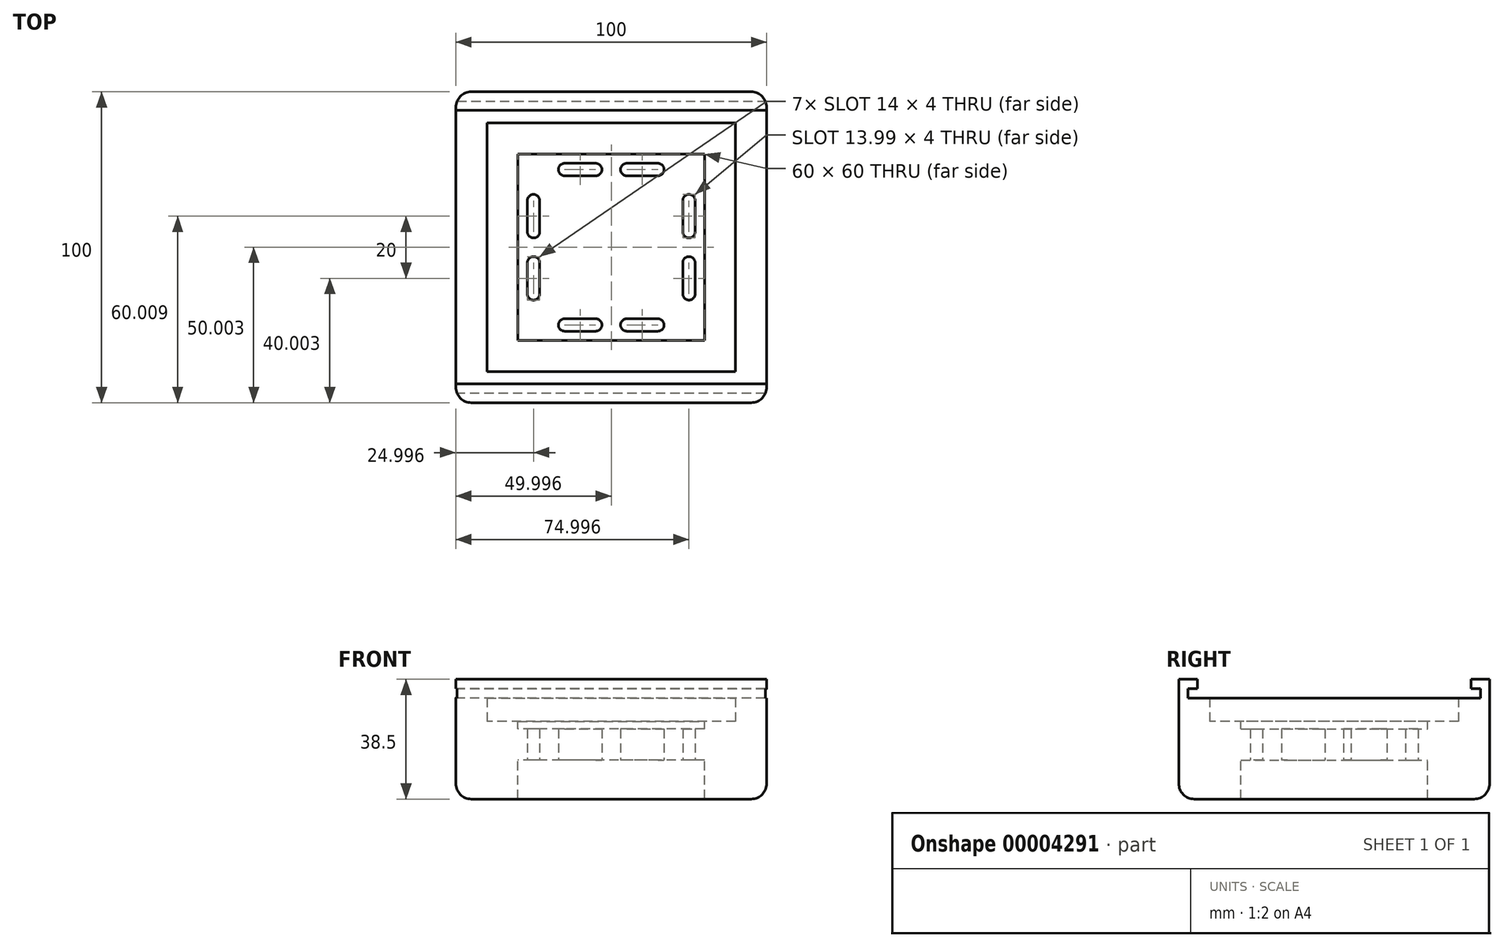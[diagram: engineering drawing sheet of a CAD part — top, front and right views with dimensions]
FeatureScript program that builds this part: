
annotation { "Feature Type Name" : "Feature", "Feature Type Description" : "" }
export const myFeature = defineFeature(function(context is Context, id is Id, definition is map)
    precondition{}
    {
        {
            var Q0;
            Q0=qCreatedBy(makeId("Top.planeOp"),FACE);
            var sketch = newSketch(context, id + "F0", { "sketchPlane" : qUnion([Q0])});
            skLineSegment(sketch, "E0", {"start": v(-127.44, -55.42) * mm, "end": v(-127.44, 44.58) * mm});
            skLineSegment(sketch, "E1", {"start": v(-127.44, 44.58) * mm, "end": v(-27.44, 44.58) * mm});
            skLineSegment(sketch, "E2", {"start": v(-27.44, 44.58) * mm, "end": v(-27.44, -55.42) * mm});
            skLineSegment(sketch, "E3", {"start": v(-27.44, -55.42) * mm, "end": v(-127.44, -55.42) * mm});
            skSolve(sketch);
        }
        {
            var Q0;
            Q0=makeQuery(id+"F0.imprint","IMPRINT",FACE,{"disambiguationData":[TD([[makeQuery(id+"F0.imprint","IMPRINT",EDGE,{"derivedFrom":sQuery(id+"F0.wireOp",EDGE,"E0")}),-1.0]])]});
            extrude(context, id + "F1", {"entities" : qUnion([Q0]), "depth" : 10 * mm});
        }
        {
            var Q0;
            Q0=makeQuery(id+"F1.opExtrude","CAP_FACE",FACE,{"disambiguationData":[OSD([sQuery(id+"F0.wireOp",EDGE,"E0"),sQuery(id+"F0.wireOp",EDGE,"E1"),sQuery(id+"F0.wireOp",EDGE,"E2"),sQuery(id+"F0.wireOp",EDGE,"E3")])],"isStart":false});
            var sketch = newSketch(context, id + "F2", { "sketchPlane" : qUnion([Q0])});
            skLineSegment(sketch, "E4.0", {"start": v(-117.44, 34.58) * mm, "end": v(-37.44, 34.58) * mm});
            skLineSegment(sketch, "E4.1", {"start": v(-117.44, -45.42) * mm, "end": v(-117.44, 34.58) * mm});
            skLineSegment(sketch, "E4.2", {"start": v(-37.44, -45.42) * mm, "end": v(-117.44, -45.42) * mm});
            skLineSegment(sketch, "E4.3", {"start": v(-37.44, 34.58) * mm, "end": v(-37.44, -45.42) * mm});
            skSolve(sketch);
        }
        {
            var Q0;
            Q0=makeQuery(id+"F2.imprint","IMPRINT",FACE,{"disambiguationData":[TD([[makeQuery(id+"F2.imprint","IMPRINT",EDGE,{"derivedFrom":sQuery(id+"F2.wireOp",EDGE,"E4.0")}),1.0]])]});
            extrude(context, id + "F3", {"entities" : qUnion([Q0]), "operationType" : NewBodyOperationType.ADD, "depth" : 10 * mm});
        }
        {
            var Q0;
            Q0=makeQuery(id+"F1.opExtrude","CAP_FACE",FACE,{"disambiguationData":[OSD([sQuery(id+"F0.wireOp",EDGE,"E0"),sQuery(id+"F0.wireOp",EDGE,"E1"),sQuery(id+"F0.wireOp",EDGE,"E2"),sQuery(id+"F0.wireOp",EDGE,"E3")])],"isStart":true});
            var sketch = newSketch(context, id + "F4", { "sketchPlane" : qUnion([Q0])});
            skLineSegment(sketch, "E5.0", {"start": v(-107.44, 35.42) * mm, "end": v(-107.44, -24.58) * mm});
            skLineSegment(sketch, "E5.1", {"start": v(-47.44, 35.42) * mm, "end": v(-107.44, 35.42) * mm});
            skLineSegment(sketch, "E5.2", {"start": v(-47.44, -24.58) * mm, "end": v(-47.44, 35.42) * mm});
            skLineSegment(sketch, "E5.3", {"start": v(-107.44, -24.58) * mm, "end": v(-47.44, -24.58) * mm});
            skLineSegment(sketch, "E6.0", {"start": v(-97.44, 25.42) * mm, "end": v(-97.44, -14.58) * mm});
            skLineSegment(sketch, "E6.1", {"start": v(-57.44, 25.42) * mm, "end": v(-97.44, 25.42) * mm});
            skLineSegment(sketch, "E6.2", {"start": v(-57.44, -14.58) * mm, "end": v(-57.44, 25.42) * mm});
            skLineSegment(sketch, "E6.3", {"start": v(-97.44, -14.58) * mm, "end": v(-57.44, -14.58) * mm});
            skSolve(sketch);
        }
        {
            var Q0;
            Q0=makeQuery(id+"F4.imprint","IMPRINT",FACE,{"disambiguationData":[TD([[makeQuery(id+"F4.imprint","IMPRINT",EDGE,{"derivedFrom":sQuery(id+"F4.wireOp",EDGE,"E5.0")}),-1.0]])]});
            extrude(context, id + "F5", {"entities" : qUnion([Q0]), "operationType" : NewBodyOperationType.ADD, "endBound" : BoundingType.SYMMETRIC, "depth" : 25 * mm});
        }
        {
            var Q0;
            Q0=makeQuery(id+"F1.opExtrude","CAP_FACE",FACE,{"disambiguationData":[OSD([sQuery(id+"F0.wireOp",EDGE,"E0"),sQuery(id+"F0.wireOp",EDGE,"E1"),sQuery(id+"F0.wireOp",EDGE,"E2"),sQuery(id+"F0.wireOp",EDGE,"E3")])],"isStart":true});
            var sketch = newSketch(context, id + "F6", { "sketchPlane" : qUnion([Q0])});
            skLineSegment(sketch, "E7.0", {"start": v(-62.44, 32.42) * mm, "end": v(-72.44, 32.42) * mm});
            skLineSegment(sketch, "E8.0", {"start": v(-104.44, 20.42) * mm, "end": v(-104.44, 10.42) * mm});
            skLineSegment(sketch, "E9.0", {"start": v(-100.44, 20.42) * mm, "end": v(-100.44, 10.42) * mm});
            skLineSegment(sketch, "E10.0", {"start": v(-92.44, -21.58) * mm, "end": v(-82.44, -21.58) * mm});
            skLineSegment(sketch, "E11", {"start": v(-107.44, 35.42) * mm, "end": v(-107.44, -24.58) * mm});
            skLineSegment(sketch, "E12", {"start": v(-107.44, -24.58) * mm, "end": v(-47.44, -24.58) * mm});
            skLineSegment(sketch, "E13", {"start": v(-47.44, -24.58) * mm, "end": v(-47.44, 35.42) * mm});
            skArc(sketch, "E14", {"start": v(-104.44, -9.58) * mm, "mid": v(-102.44, -11.58) * mm, "end": v(-100.44, -9.58) * mm});
            skArc(sketch, "E15", {"start": v(-100.44, 0.42) * mm, "mid": v(-102.44, 2.42) * mm, "end": v(-104.44, 0.42) * mm});
            skArc(sketch, "E16", {"start": v(-104.44, 10.42) * mm, "mid": v(-102.44, 8.42) * mm, "end": v(-100.44, 10.42) * mm});
            skArc(sketch, "E17", {"start": v(-100.44, 20.42) * mm, "mid": v(-102.44, 22.42) * mm, "end": v(-104.44, 20.42) * mm});
            skArc(sketch, "E18", {"start": v(-92.44, 32.42) * mm, "mid": v(-94.44, 30.42) * mm, "end": v(-92.44, 28.42) * mm});
            skArc(sketch, "E19", {"start": v(-82.44, 28.42) * mm, "mid": v(-80.44, 30.42) * mm, "end": v(-82.44, 32.42) * mm});
            skArc(sketch, "E20", {"start": v(-72.44, 32.42) * mm, "mid": v(-74.44, 30.42) * mm, "end": v(-72.44, 28.42) * mm});
            skArc(sketch, "E21", {"start": v(-62.44, 28.42) * mm, "mid": v(-60.44, 30.42) * mm, "end": v(-62.44, 32.42) * mm});
            skArc(sketch, "E22", {"start": v(-50.44, 20.42) * mm, "mid": v(-52.44, 22.42) * mm, "end": v(-54.44, 20.42) * mm});
            skArc(sketch, "E23", {"start": v(-54.44, 10.42) * mm, "mid": v(-52.44, 8.42) * mm, "end": v(-50.44, 10.42) * mm});
            skArc(sketch, "E24", {"start": v(-50.49, 0) * mm, "mid": v(-52.23, 2.4) * mm, "end": v(-54.44, 0.42) * mm});
            skArc(sketch, "E25", {"start": v(-54.44, -9.58) * mm, "mid": v(-52.44, -11.58) * mm, "end": v(-50.44, -9.57) * mm});
            skArc(sketch, "E26", {"start": v(-62.44, -21.58) * mm, "mid": v(-60.44, -19.58) * mm, "end": v(-62.44, -17.58) * mm});
            skArc(sketch, "E27", {"start": v(-72.44, -17.58) * mm, "mid": v(-74.44, -19.58) * mm, "end": v(-72.44, -21.58) * mm});
            skArc(sketch, "E28", {"start": v(-82.44, -21.58) * mm, "mid": v(-80.44, -19.58) * mm, "end": v(-82.44, -17.58) * mm});
            skArc(sketch, "E29", {"start": v(-92.44, -17.58) * mm, "mid": v(-94.44, -19.58) * mm, "end": v(-92.44, -21.58) * mm});
            skLineSegment(sketch, "E30.trimOffspring", {"start": v(-82.44, 32.42) * mm, "end": v(-92.44, 32.42) * mm});
            skLineSegment(sketch, "E31.trimOffspring", {"start": v(-82.44, 28.42) * mm, "end": v(-92.44, 28.42) * mm});
            skLineSegment(sketch, "E32.trimOffspring", {"start": v(-62.44, 28.42) * mm, "end": v(-72.44, 28.42) * mm});
            skLineSegment(sketch, "E33.trimOffspring", {"start": v(-54.44, 10.42) * mm, "end": v(-54.44, 20.42) * mm});
            skLineSegment(sketch, "E34.trimOffspring", {"start": v(-50.44, 10.42) * mm, "end": v(-50.44, 20.42) * mm});
            skLineSegment(sketch, "E35.trimOffspring", {"start": v(-72.44, -17.58) * mm, "end": v(-62.44, -17.58) * mm});
            skLineSegment(sketch, "E36.trimOffspring", {"start": v(-72.44, -21.58) * mm, "end": v(-62.44, -21.58) * mm});
            skLineSegment(sketch, "E37.trimOffspring", {"start": v(-92.44, -17.58) * mm, "end": v(-82.44, -17.58) * mm});
            skLineSegment(sketch, "E38.trimOffspring", {"start": v(-100.44, 0.42) * mm, "end": v(-100.44, -9.58) * mm});
            skLineSegment(sketch, "E39.trimOffspring", {"start": v(-104.44, 0.42) * mm, "end": v(-104.44, -9.58) * mm});
            skLineSegment(sketch, "E40", {"start": v(-54.44, 0.42) * mm, "end": v(-54.44, -9.58) * mm});
            skLineSegment(sketch, "E41", {"start": v(-50.49, 0) * mm, "end": v(-50.44, -9.57) * mm});
            skSolve(sketch);
        }
        {
            var Q0;
            Q0=makeQuery(id+"F6.imprint","IMPRINT",FACE,{"disambiguationData":[TD([[makeQuery(id+"F6.imprint","IMPRINT",EDGE,{"derivedFrom":sQuery(id+"F6.wireOp",EDGE,"E8.0")}),1.0]])]});
            var Q1;
            Q1=makeQuery(id+"F6.imprint","IMPRINT",FACE,{"disambiguationData":[TD([[makeQuery(id+"F6.imprint","IMPRINT",EDGE,{"derivedFrom":sQuery(id+"F6.wireOp",EDGE,"E18")}),1.0]])]});
            var Q2;
            Q2=makeQuery(id+"F6.imprint","IMPRINT",FACE,{"disambiguationData":[TD([[makeQuery(id+"F6.imprint","IMPRINT",EDGE,{"derivedFrom":sQuery(id+"F6.wireOp",EDGE,"E7.0")}),1.0]])]});
            var Q3;
            Q3=makeQuery(id+"F6.imprint","IMPRINT",FACE,{"disambiguationData":[TD([[makeQuery(id+"F6.imprint","IMPRINT",EDGE,{"derivedFrom":sQuery(id+"F6.wireOp",EDGE,"E22")}),1.0]])]});
            var Q4;
            Q4=makeQuery(id+"F6.imprint","IMPRINT",FACE,{"disambiguationData":[TD([[makeQuery(id+"F6.imprint","IMPRINT",EDGE,{"derivedFrom":sQuery(id+"F6.wireOp",EDGE,"E24")}),1.0]])]});
            var Q5;
            Q5=makeQuery(id+"F6.imprint","IMPRINT",FACE,{"disambiguationData":[TD([[makeQuery(id+"F6.imprint","IMPRINT",EDGE,{"derivedFrom":sQuery(id+"F6.wireOp",EDGE,"E26")}),1.0]])]});
            var Q6;
            Q6=makeQuery(id+"F6.imprint","IMPRINT",FACE,{"disambiguationData":[TD([[makeQuery(id+"F6.imprint","IMPRINT",EDGE,{"derivedFrom":sQuery(id+"F6.wireOp",EDGE,"E10.0")}),1.0]])]});
            var Q7;
            Q7=makeQuery(id+"F6.imprint","IMPRINT",FACE,{"disambiguationData":[TD([[makeQuery(id+"F6.imprint","IMPRINT",EDGE,{"derivedFrom":sQuery(id+"F6.wireOp",EDGE,"E14")}),1.0]])]});
            extrude(context, id + "F7", {"entities" : qUnion([Q0, Q1, Q2, Q3, Q4, Q5, Q6, Q7]), "operationType" : NewBodyOperationType.REMOVE, "oppositeDirection" : true, "depth" : 42.57 * mm});
        }
        {
            var Q0;
            Q0=makeQuery(id+"F3.opExtrude","CAP_FACE",FACE,{"disambiguationData":[OSD([sQuery(id+"F0.wireOp",EDGE,"E0"),sQuery(id+"F0.wireOp",EDGE,"E1"),sQuery(id+"F0.wireOp",EDGE,"E2"),sQuery(id+"F0.wireOp",EDGE,"E3"),sQuery(id+"F2.wireOp",EDGE,"E4.0"),sQuery(id+"F2.wireOp",EDGE,"E4.1"),sQuery(id+"F2.wireOp",EDGE,"E4.2"),sQuery(id+"F2.wireOp",EDGE,"E4.3")])],"isStart":false});
            var sketch = newSketch(context, id + "F8", { "sketchPlane" : qUnion([Q0])});
            skLineSegment(sketch, "E42.0", {"start": v(-27.44, -52.42) * mm, "end": v(-127.44, -52.42) * mm});
            skLineSegment(sketch, "E43.0", {"start": v(-127.44, 41.58) * mm, "end": v(-27.44, 41.58) * mm});
            skSolve(sketch);
        }
        {
            var Q0;
            {var subQ1=sQuery(id+"F8.wireOp",EDGE,"E42.0");Q0=makeQuery(id+"F8.imprint","IMPRINT",FACE,{"disambiguationData":[TD([[makeQuery(id+"F8.imprint","IMPRINT",EDGE,{"derivedFrom":subQ1}),1.0]])]});}
            var Q1;
            {var subQ1=sQuery(id+"F8.wireOp",EDGE,"E43.0");Q1=makeQuery(id+"F8.imprint","IMPRINT",FACE,{"disambiguationData":[TD([[makeQuery(id+"F8.imprint","IMPRINT",EDGE,{"derivedFrom":subQ1}),1.0]])]});}
            extrude(context, id + "F9", {"entities" : qUnion([Q0, Q1]), "operationType" : NewBodyOperationType.ADD, "depth" : 6 * mm});
        }
        {
            var Q0;
            Q0=makeQuery(id+"F9.opExtrude","SWEPT_FACE",FACE,{"disambiguationData":[OSD([sQuery(id+"F8.wireOp",EDGE,"E43.0")])]});
            var sketch = newSketch(context, id + "F10", { "sketchPlane" : qUnion([Q0])});
            skLineSegment(sketch, "E44.0", {"start": v(-127.44, 23) * mm, "end": v(-27.44, 23) * mm});
            skSolve(sketch);
        }
        {
            var Q0;
            {var subQ2=sQuery(id+"F10.wireOp",EDGE,"E44.0");Q0=makeQuery(id+"F10.imprint","IMPRINT",FACE,{"disambiguationData":[TD([[makeQuery(id+"F10.imprint","IMPRINT",EDGE,{"derivedFrom":subQ2}),1.0]])]});}
            extrude(context, id + "F11", {"entities" : qUnion([Q0]), "operationType" : NewBodyOperationType.ADD, "depth" : 3 * mm});
        }
        {
            var Q0;
            Q0=makeQuery(id+"F9.opExtrude","SWEPT_FACE",FACE,{"disambiguationData":[OSD([sQuery(id+"F8.wireOp",EDGE,"E42.0")])]});
            var sketch = newSketch(context, id + "F12", { "sketchPlane" : qUnion([Q0])});
            skLineSegment(sketch, "E45.0", {"start": v(27.44, 23) * mm, "end": v(127.44, 23) * mm});
            skSolve(sketch);
        }
        {
            var Q0;
            {var subQ2=sQuery(id+"F12.wireOp",EDGE,"E45.0");Q0=makeQuery(id+"F12.imprint","IMPRINT",FACE,{"disambiguationData":[TD([[makeQuery(id+"F12.imprint","IMPRINT",EDGE,{"derivedFrom":subQ2}),1.0]])]});}
            extrude(context, id + "F13", {"entities" : qUnion([Q0]), "operationType" : NewBodyOperationType.ADD, "depth" : 3 * mm});
        }
        {
            var Q0;
            Q0=makeQuery(id+"F5.opExtrude","CAP_EDGE",EDGE,{"disambiguationData":[OSD([sQuery(id+"F0.wireOp",EDGE,"E3")])],"isStart":false});
            var Q1;
            Q1=makeQuery(id+"F5.opExtrude","CAP_EDGE",EDGE,{"disambiguationData":[OSD([sQuery(id+"F0.wireOp",EDGE,"E2")])],"isStart":false});
            var Q2;
            Q2=makeQuery(id+"F5.opExtrude","CAP_EDGE",EDGE,{"disambiguationData":[OSD([sQuery(id+"F0.wireOp",EDGE,"E1")])],"isStart":false});
            var Q3;
            Q3=makeQuery(id+"F5.opExtrude","CAP_EDGE",EDGE,{"disambiguationData":[OSD([sQuery(id+"F0.wireOp",EDGE,"E0")])],"isStart":false});
            fillet(context, id + "F14", {"entities" : qUnion([Q0, Q1, Q2, Q3]), "radius" : 5 * mm, "tangentPropagation" : true, "allowEdgeOverflow" : false});
        }
        {
            var Q0;
            {var subQ0=sQuery(id+"F0.wireOp",EDGE,"E1");var subQ1=sQuery(id+"F0.wireOp",EDGE,"E2");Q0=makeQuery(id+"F9.boolean.opBoolean","MERGE",EDGE,{"derivedFrom":[makeQuery(id+"F5.boolean.opBoolean","MERGE",EDGE,{"derivedFrom":[makeQuery(id+"F3.boolean.opBoolean","MERGE",EDGE,{"derivedFrom":[makeQuery(id+"F1.opExtrude","SWEPT_EDGE",EDGE,{"disambiguationData":[OSD([subQ0,subQ1])]}),makeQuery(id+"F3.opExtrude","SWEPT_EDGE",EDGE,{"disambiguationData":[OSD([subQ0,subQ1])]})]}),makeQuery(id+"F5.opExtrude","SWEPT_EDGE",EDGE,{"disambiguationData":[OSD([subQ0,subQ1])]})]}),makeQuery(id+"F9.opExtrude","SWEPT_EDGE",EDGE,{"disambiguationData":[OSD([subQ0,subQ1])]})]});}
            var Q1;
            {var subQ0=sQuery(id+"F0.wireOp",EDGE,"E2");var subQ1=sQuery(id+"F0.wireOp",EDGE,"E3");Q1=makeQuery(id+"F9.boolean.opBoolean","MERGE",EDGE,{"derivedFrom":[makeQuery(id+"F5.boolean.opBoolean","MERGE",EDGE,{"derivedFrom":[makeQuery(id+"F3.boolean.opBoolean","MERGE",EDGE,{"derivedFrom":[makeQuery(id+"F1.opExtrude","SWEPT_EDGE",EDGE,{"disambiguationData":[OSD([subQ0,subQ1])]}),makeQuery(id+"F3.opExtrude","SWEPT_EDGE",EDGE,{"disambiguationData":[OSD([subQ0,subQ1])]})]}),makeQuery(id+"F5.opExtrude","SWEPT_EDGE",EDGE,{"disambiguationData":[OSD([subQ0,subQ1])]})]}),makeQuery(id+"F9.opExtrude","SWEPT_EDGE",EDGE,{"disambiguationData":[OSD([subQ0,subQ1])]})]});}
            var Q2;
            {var subQ0=sQuery(id+"F0.wireOp",EDGE,"E0");var subQ1=sQuery(id+"F0.wireOp",EDGE,"E1");Q2=makeQuery(id+"F9.boolean.opBoolean","MERGE",EDGE,{"derivedFrom":[makeQuery(id+"F5.boolean.opBoolean","MERGE",EDGE,{"derivedFrom":[makeQuery(id+"F3.boolean.opBoolean","MERGE",EDGE,{"derivedFrom":[makeQuery(id+"F1.opExtrude","SWEPT_EDGE",EDGE,{"disambiguationData":[OSD([subQ0,subQ1])]}),makeQuery(id+"F3.opExtrude","SWEPT_EDGE",EDGE,{"disambiguationData":[OSD([subQ0,subQ1])]})]}),makeQuery(id+"F5.opExtrude","SWEPT_EDGE",EDGE,{"disambiguationData":[OSD([subQ0,subQ1])]})]}),makeQuery(id+"F9.opExtrude","SWEPT_EDGE",EDGE,{"disambiguationData":[OSD([subQ0,subQ1])]})]});}
            var Q3;
            {var subQ0=sQuery(id+"F0.wireOp",EDGE,"E0");var subQ1=sQuery(id+"F0.wireOp",EDGE,"E3");Q3=makeQuery(id+"F9.boolean.opBoolean","MERGE",EDGE,{"derivedFrom":[makeQuery(id+"F5.boolean.opBoolean","MERGE",EDGE,{"derivedFrom":[makeQuery(id+"F3.boolean.opBoolean","MERGE",EDGE,{"derivedFrom":[makeQuery(id+"F1.opExtrude","SWEPT_EDGE",EDGE,{"disambiguationData":[OSD([subQ0,subQ1])]}),makeQuery(id+"F3.opExtrude","SWEPT_EDGE",EDGE,{"disambiguationData":[OSD([subQ0,subQ1])]})]}),makeQuery(id+"F5.opExtrude","SWEPT_EDGE",EDGE,{"disambiguationData":[OSD([subQ0,subQ1])]})]}),makeQuery(id+"F9.opExtrude","SWEPT_EDGE",EDGE,{"disambiguationData":[OSD([subQ0,subQ1])]})]});}
            fillet(context, id + "F15", {"entities" : qUnion([Q0, Q1, Q2, Q3]), "radius" : 5 * mm, "tangentPropagation" : true, "allowEdgeOverflow" : false});
        }
    });
